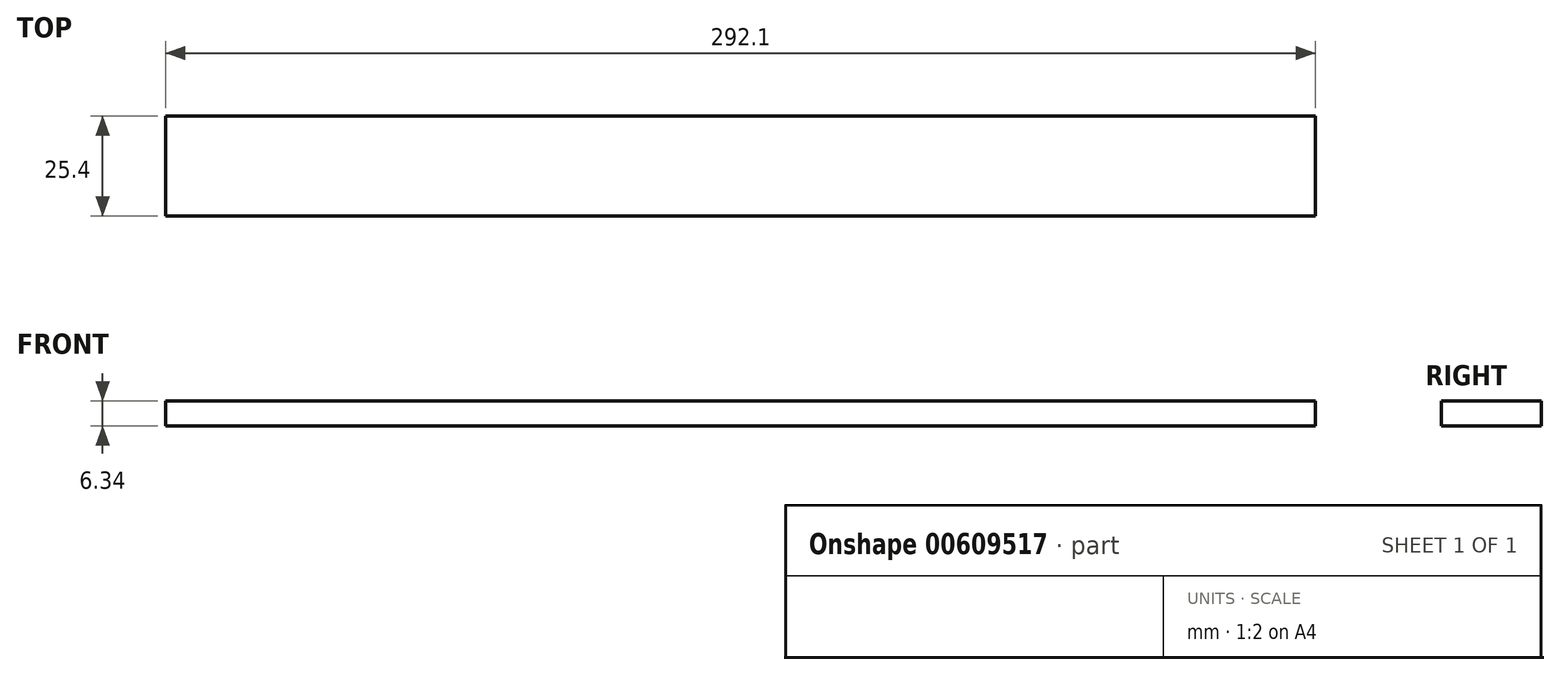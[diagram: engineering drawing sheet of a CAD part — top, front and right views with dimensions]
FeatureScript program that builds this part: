
annotation { "Feature Type Name" : "Feature", "Feature Type Description" : "" }
export const myFeature = defineFeature(function(context is Context, id is Id, definition is map)
    precondition{}
    {
        {
            var Q0;
            Q0=qCreatedBy(makeId("Front.planeOp"),FACE);
            var sketch = newSketch(context, id + "F0", { "sketchPlane" : qUnion([Q0])});
            skLineSegment(sketch, "E0.bottom", {"start": v(-146.05, 3.18) * mm, "end": v(146.05, 3.18) * mm});
            skLineSegment(sketch, "E0.top", {"start": v(-146.05, -3.18) * mm, "end": v(146.05, -3.18) * mm});
            skLineSegment(sketch, "E0.left", {"start": v(-146.05, 3.18) * mm, "end": v(-146.05, -3.17) * mm});
            skLineSegment(sketch, "E0.right", {"start": v(146.05, 3.17) * mm, "end": v(146.05, -3.17) * mm});
            skPoint(sketch, "E0.middle", {"position": v(0, 0) * mm});
            skSolve(sketch);
        }
        {
            var Q0;
            Q0 = qSketchRegion(id + "F0", true);
            extrude(context, id + "F1", {"entities" : qUnion([Q0]), "depth" : 25.4 * mm, "offsetDistance" : 25.4 * mm});
        }
    });
